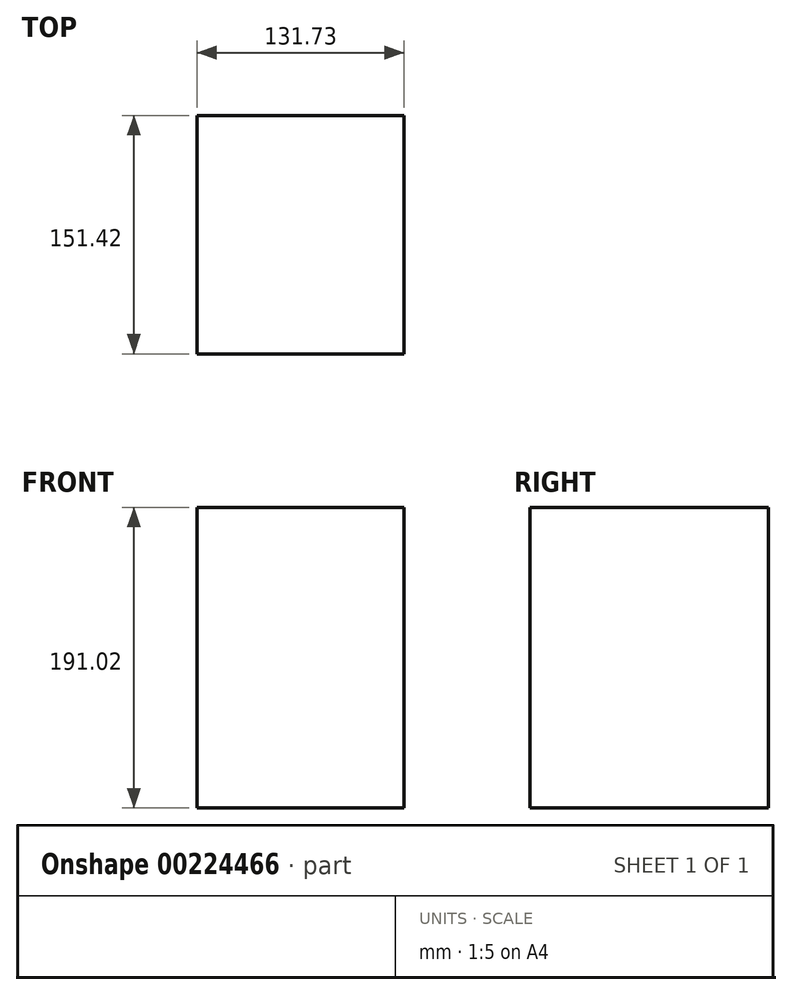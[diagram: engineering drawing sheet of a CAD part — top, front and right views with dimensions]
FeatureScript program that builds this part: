
annotation { "Feature Type Name" : "Feature", "Feature Type Description" : "" }
export const myFeature = defineFeature(function(context is Context, id is Id, definition is map)
    precondition{}
    {
        {
            var Q0;
            Q0=qCreatedBy(makeId("Front.planeOp"),FACE);
            var sketch = newSketch(context, id + "F0", { "sketchPlane" : qUnion([Q0])});
            skLineSegment(sketch, "E0.bottom", {"start": v(-59.33, 82.62) * mm, "end": v(47, 82.62) * mm});
            skLineSegment(sketch, "E0.top", {"start": v(-59.33, -108.4) * mm, "end": v(47, -108.4) * mm});
            skLineSegment(sketch, "E0.left", {"start": v(-59.33, 82.62) * mm, "end": v(-59.33, -108.4) * mm});
            skLineSegment(sketch, "E0.right", {"start": v(47, 82.62) * mm, "end": v(47, -108.4) * mm});
            skSolve(sketch);
        }
        {
            var Q0;
            Q0 = qSketchRegion(id + "F0", true);
            extrude(context, id + "F1", {"entities" : qUnion([Q0]), "depth" : 25.4 * mm});
        }
        {
            var Q0;
            Q0=makeQuery(id+"F1.opExtrude","CAP_FACE",FACE,{"disambiguationData":[OSD([sQuery(id+"F0.wireOp",EDGE,"E0.bottom"),sQuery(id+"F0.wireOp",EDGE,"E0.top"),sQuery(id+"F0.wireOp",EDGE,"E0.left"),sQuery(id+"F0.wireOp",EDGE,"E0.right")])],"isStart":false});
            extrude(context, id + "F5", {"entities" : qUnion([Q0]), "operationType" : NewBodyOperationType.ADD, "depth" : 100.62 * mm});
        }
        {
            var Q0;
            {var subQ0=sQuery(id+"F0.wireOp",EDGE,"E0.right");Q0=makeQuery(id+"F5.boolean.opBoolean","MERGE",FACE,{"derivedFrom":[makeQuery(id+"F1.opExtrude","SWEPT_FACE",FACE,{"disambiguationData":[OSD([subQ0])]}),makeQuery(id+"F5.opExtrude","SWEPT_FACE",FACE,{"disambiguationData":[OSD([subQ0])]})]});}
            extrude(context, id + "F2", {"entities" : qUnion([Q0]), "operationType" : NewBodyOperationType.ADD, "depth" : 25.4 * mm});
        }
        {
            var Q0;
            {var subQ0=sQuery(id+"F0.wireOp",EDGE,"E0.right");Q0=makeQuery(id+"F2.boolean.opBoolean","MERGE",FACE,{"derivedFrom":[makeQuery(id+"F1.opExtrude","CAP_FACE",FACE,{"disambiguationData":[OSD([sQuery(id+"F0.wireOp",EDGE,"E0.bottom"),sQuery(id+"F0.wireOp",EDGE,"E0.top"),sQuery(id+"F0.wireOp",EDGE,"E0.left"),subQ0])],"isStart":true}),makeQuery(id+"F2.opExtrude","SWEPT_FACE",FACE,{"disambiguationData":[OSD([subQ0]),TDD([makeQuery(id+"F1.opExtrude","CAP_EDGE",EDGE,{"disambiguationData":[OSD([subQ0])],"isStart":true})])]})]});}
            extrude(context, id + "F3", {"entities" : qUnion([Q0]), "operationType" : NewBodyOperationType.ADD, "depth" : 25.4 * mm});
        }
        {
            var Q0;
            Q0=qCreatedBy(makeId("Front.planeOp"),FACE);
            var sketch = newSketch(context, id + "F6", { "sketchPlane" : qUnion([Q0])});
            skFitSpline(sketch, "E1", {"points": [v(210.4, -111.88) * mm, v(120.71, -359.82) * mm, v(-69.57, -219.2) * mm, v(-288.6, -400.46) * mm], "startDerivative": vector(-179.22, -1125.6) * mm, "endDerivative": vector(-615.68, -868.78) * mm});
            skSolve(sketch);
        }
        {
            var Q0;
            Q0 = qSketchRegion(id + "F6", true);
            var Q1;
            Q1=sQuery(id+"F6.wireOp",EDGE,"E1");
            extrude(context, id + "F4", {"entities" : qUnion([Q0]), "bodyType" : ToolBodyType.SURFACE, "surfaceEntities" : qUnion([Q1]), "depth" : 147.62 * mm});
        }
    });
